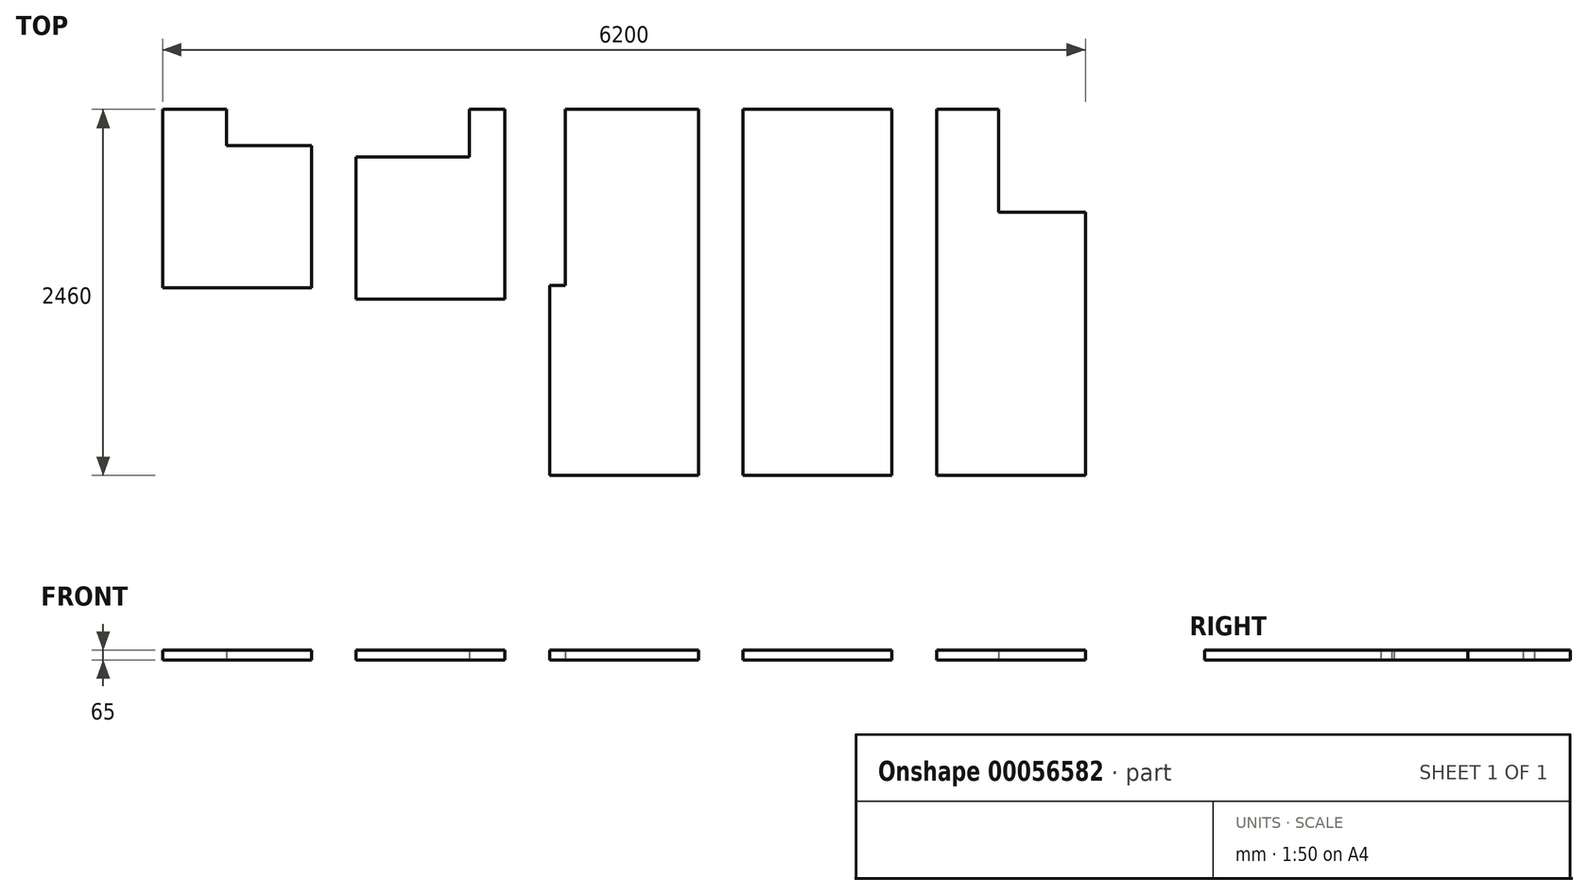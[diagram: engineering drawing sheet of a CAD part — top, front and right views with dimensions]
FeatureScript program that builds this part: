
annotation { "Feature Type Name" : "Feature", "Feature Type Description" : "" }
export const myFeature = defineFeature(function(context is Context, id is Id, definition is map)
    precondition{}
    {
        {
            var Q0;
            Q0=qCreatedBy(makeId("Top.planeOp"),FACE);
            var sketch = newSketch(context, id + "F0", { "sketchPlane" : qUnion([Q0])});
            skLineSegment(sketch, "E0.bottom", {"start": v(-554.67, 660.03) * mm, "end": v(-124.67, 660.03) * mm});
            skLineSegment(sketch, "E0.top", {"start": v(-554.67, -539.97) * mm, "end": v(445.33, -539.97) * mm});
            skLineSegment(sketch, "E0.left", {"start": v(-554.67, 660.03) * mm, "end": v(-554.67, -539.97) * mm});
            skLineSegment(sketch, "E0.right", {"start": v(445.33, 416.03) * mm, "end": v(445.33, -539.97) * mm});
            skLineSegment(sketch, "E1.top", {"start": v(445.33, 416.03) * mm, "end": v(-124.67, 416.03) * mm});
            skLineSegment(sketch, "E1.right", {"start": v(-124.67, 660.03) * mm, "end": v(-124.67, 416.03) * mm});
            skLineSegment(sketch, "E2.bottom", {"start": v(745.33, -614.97) * mm, "end": v(1745.33, -614.97) * mm});
            skLineSegment(sketch, "E2.top", {"start": v(1505.33, 660.03) * mm, "end": v(1745.33, 660.03) * mm});
            skLineSegment(sketch, "E2.left", {"start": v(745.33, -614.97) * mm, "end": v(745.33, 341.03) * mm});
            skLineSegment(sketch, "E2.right", {"start": v(1745.33, -614.97) * mm, "end": v(1745.33, 660.03) * mm});
            skLineSegment(sketch, "E3.top", {"start": v(745.33, 341.03) * mm, "end": v(1505.33, 341.03) * mm});
            skLineSegment(sketch, "E3.right", {"start": v(1505.33, 660.03) * mm, "end": v(1505.33, 341.03) * mm});
            skLineSegment(sketch, "E4.bottom", {"start": v(2150.33, 660.03) * mm, "end": v(3045.33, 660.03) * mm});
            skLineSegment(sketch, "E4.top", {"start": v(2045.33, -1799.97) * mm, "end": v(3045.33, -1799.97) * mm});
            skLineSegment(sketch, "E4.left", {"start": v(2045.33, -524.97) * mm, "end": v(2045.33, -1799.97) * mm});
            skLineSegment(sketch, "E4.right", {"start": v(3045.33, 660.03) * mm, "end": v(3045.33, -1799.97) * mm});
            skLineSegment(sketch, "E5.top", {"start": v(2045.33, -524.97) * mm, "end": v(2150.33, -524.97) * mm});
            skLineSegment(sketch, "E5.right", {"start": v(2150.33, 660.03) * mm, "end": v(2150.33, -524.97) * mm});
            skLineSegment(sketch, "E6.bottom", {"start": v(3345.33, 660.03) * mm, "end": v(4345.33, 660.03) * mm});
            skLineSegment(sketch, "E6.top", {"start": v(3345.33, -1799.97) * mm, "end": v(4345.33, -1799.97) * mm});
            skLineSegment(sketch, "E6.left", {"start": v(3345.33, 660.03) * mm, "end": v(3345.33, -1799.97) * mm});
            skLineSegment(sketch, "E6.right", {"start": v(4345.33, 660.03) * mm, "end": v(4345.33, -1799.97) * mm});
            skLineSegment(sketch, "E7.bottom", {"start": v(4645.33, 660.03) * mm, "end": v(5063.33, 660.03) * mm});
            skLineSegment(sketch, "E7.top", {"start": v(4645.33, -1799.97) * mm, "end": v(5645.33, -1799.97) * mm});
            skLineSegment(sketch, "E7.left", {"start": v(4645.33, 660.03) * mm, "end": v(4645.33, -1799.97) * mm});
            skLineSegment(sketch, "E7.right", {"start": v(5645.33, -29.97) * mm, "end": v(5645.33, -1799.97) * mm});
            skLineSegment(sketch, "E8.top", {"start": v(5645.33, -29.97) * mm, "end": v(5063.33, -29.97) * mm});
            skLineSegment(sketch, "E8.right", {"start": v(5063.33, 660.03) * mm, "end": v(5063.33, -29.97) * mm});
            skSolve(sketch);
        }
        {
            var Q0;
            Q0 = qSketchRegion(id + "F0", true);
            extrude(context, id + "F1", {"entities" : qUnion([Q0]), "depth" : 65 * mm});
        }
    });
